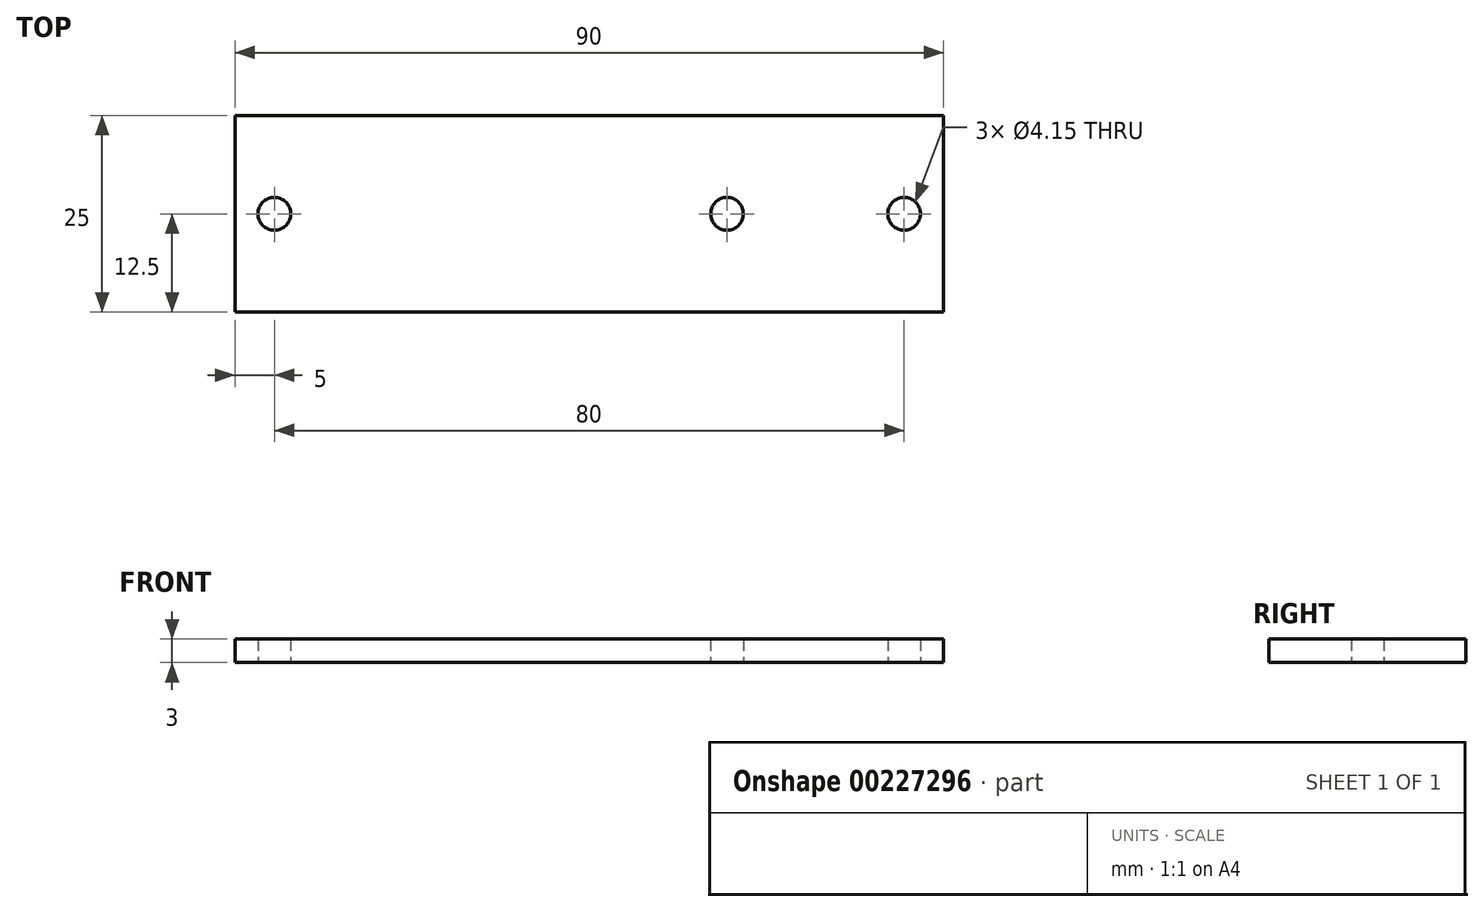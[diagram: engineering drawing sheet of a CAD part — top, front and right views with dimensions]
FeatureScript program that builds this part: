
annotation { "Feature Type Name" : "Feature", "Feature Type Description" : "" }
export const myFeature = defineFeature(function(context is Context, id is Id, definition is map)
    precondition{}
    {
        {
            var Q0;
            Q0=qCreatedBy(makeId("Top.planeOp"),FACE);
            var sketch = newSketch(context, id + "F0", { "sketchPlane" : qUnion([Q0])});
            skLineSegment(sketch, "E0.bottom", {"start": v(-45, 12.5) * mm, "end": v(45, 12.5) * mm});
            skLineSegment(sketch, "E0.top", {"start": v(-45, -12.5) * mm, "end": v(45, -12.5) * mm});
            skLineSegment(sketch, "E0.left", {"start": v(-45, 12.5) * mm, "end": v(-45, -12.5) * mm});
            skLineSegment(sketch, "E0.right", {"start": v(45, 12.5) * mm, "end": v(45, -12.5) * mm});
            skLineSegment(sketch, "E1", {"start": v(-45, -12.5) * mm, "end": v(45, 12.5) * mm, "construction": true});
            skCircle(sketch, "E2", {"center": v(-40, 0) * mm, "radius": 2.08 * mm});
            skCircle(sketch, "E3", {"center": v(17.5, 0) * mm, "radius": 2.08 * mm});
            skCircle(sketch, "E4", {"center": v(40, 0) * mm, "radius": 2.08 * mm});
            skSolve(sketch);
        }
        {
            var Q0;
            Q0 = qSketchRegion(id + "F0", true);
            extrude(context, id + "F1", {"entities" : qUnion([Q0]), "depth" : 3 * mm});
        }
    });
